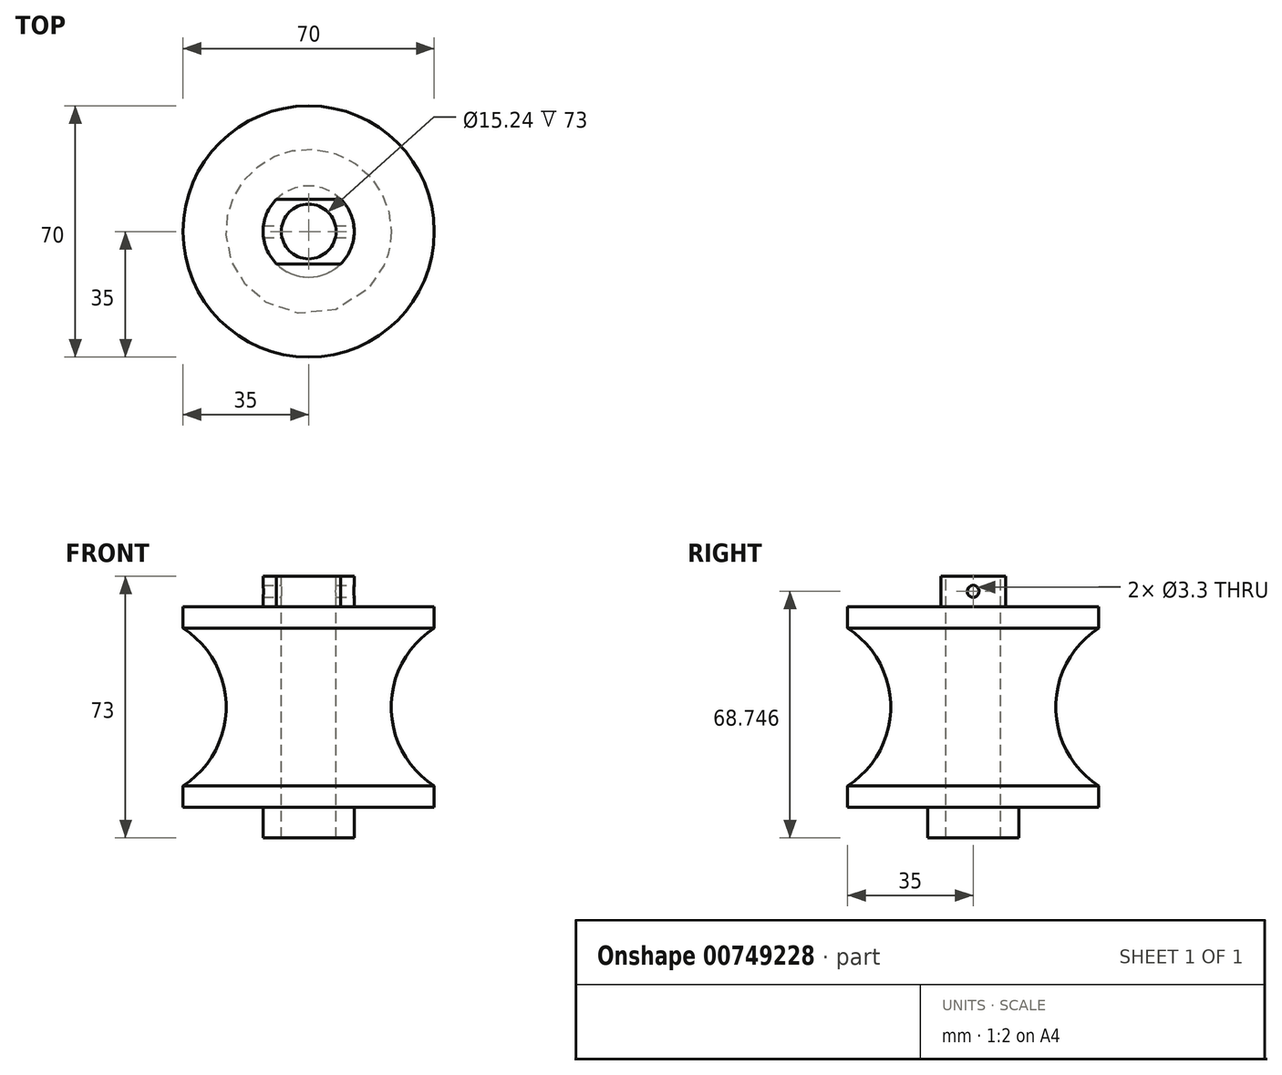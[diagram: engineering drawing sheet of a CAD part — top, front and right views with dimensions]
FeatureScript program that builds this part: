
annotation { "Feature Type Name" : "Feature", "Feature Type Description" : "" }
export const myFeature = defineFeature(function(context is Context, id is Id, definition is map)
    precondition{}
    {
        {
            var Q0;
            Q0=qCreatedBy(makeId("Front.planeOp"),FACE);
            var sketch = newSketch(context, id + "F0", { "sketchPlane" : qUnion([Q0])});
            skLineSegment(sketch, "E0", {"start": v(0, 27.87) * mm, "end": v(0, -28.13) * mm});
            skLineSegment(sketch, "E1", {"start": v(0, 27.87) * mm, "end": v(-35, 27.87) * mm});
            skLineSegment(sketch, "E2", {"start": v(-35, 27.87) * mm, "end": v(-35, 21.87) * mm});
            skLineSegment(sketch, "E3", {"start": v(-35, -22.13) * mm, "end": v(-35, -28.13) * mm});
            skLineSegment(sketch, "E4", {"start": v(-35, -28.13) * mm, "end": v(0, -28.13) * mm});
            skArc(sketch, "E5", {"start": v(-35, -22.13) * mm, "mid": v(-23, -0.13) * mm, "end": v(-35, 21.87) * mm});
            skPoint(sketch, "E6", {"position": v(-23, -0.13) * mm});
            skPoint(sketch, "E7.orphan", {"position": v(0, 36.76) * mm});
            skSolve(sketch);
        }
        {
            var Q0;
            Q0 = qSketchRegion(id + "F0", true);
            var Q1;
            Q1=sQuery(id+"F0.wireOp",EDGE,"E0");
            revolve(context, id + "F1", {"surfaceOperationType" : NewSurfaceOperationType.NEW, "entities" : qUnion([Q0]), "axis" : qUnion([Q1]), "revolveType" : RevolveType.FULL});
        }
        {
            var Q0;
            Q0=makeQuery(id+"F1.opRevolve","SWEPT_FACE",FACE,{"disambiguationData":[OSD([sQuery(id+"F0.wireOp",EDGE,"E1")])]});
            cPlane(context, id + "F2", {"entities" : qUnion([Q0]), "cplaneType" : CPlaneType.OFFSET, "offset" : 8.5 * mm, "width" : 150 * mm, "height" : 150 * mm});
        }
        {
            var Q0;
            Q0=qCreatedBy(id+"F2.planeOp",FACE);
            var sketch = newSketch(context, id + "F3", { "sketchPlane" : qUnion([Q0])});
            skCircle(sketch, "E8", {"center": v(0, 0) * mm, "radius": 12.7 * mm});
            skSolve(sketch);
        }
        {
            var Q0;
            Q0 = qSketchRegion(id + "F3", true);
            extrude(context, id + "F4", {"entities" : qUnion([Q0]), "operationType" : NewBodyOperationType.REMOVE, "endBound" : BoundingType.THROUGH_ALL, "oppositeDirection" : true, "depth" : 25 * mm, "offsetDistance" : 25 * mm});
        }
        {
            var Q0;
            Q0 = qSketchRegion(id + "F3", true);
            extrude(context, id + "F5", {"entities" : qUnion([Q0]), "operationType" : NewBodyOperationType.ADD, "oppositeDirection" : true, "depth" : 73 * mm, "offsetDistance" : 25.4 * mm});
        }
        {
            var Q0;
            Q0=makeQuery(id+"F5.opExtrude","CAP_FACE",FACE,{"disambiguationData":[OSD([sQuery(id+"F3.wireOp",EDGE,"E8")])],"isStart":true});
            var sketch = newSketch(context, id + "F6", { "sketchPlane" : qUnion([Q0])});
            skCircle(sketch, "E9", {"center": v(0, 0) * mm, "radius": 7.62 * mm});
            skSolve(sketch);
        }
        {
            var Q0;
            Q0 = qSketchRegion(id + "F6", true);
            extrude(context, id + "F7", {"entities" : qUnion([Q0]), "operationType" : NewBodyOperationType.REMOVE, "endBound" : BoundingType.THROUGH_ALL, "oppositeDirection" : true, "depth" : 25.4 * mm, "offsetDistance" : 25.4 * mm});
        }
        {
            var Q0;
            Q0=makeQuery(id+"F5.opExtrude","CAP_FACE",FACE,{"disambiguationData":[OSD([sQuery(id+"F3.wireOp",EDGE,"E8")])],"isStart":true});
            var sketch = newSketch(context, id + "F8", { "sketchPlane" : qUnion([Q0])});
            skLineSegment(sketch, "E10.bottom", {"start": v(15, -9) * mm, "end": v(-15, -9) * mm});
            skLineSegment(sketch, "E10.top", {"start": v(15, 9) * mm, "end": v(-15, 9) * mm});
            skPoint(sketch, "E10.middle", {"position": v(0, 0) * mm});
            skLineSegment(sketch, "E11", {"start": v(-15, 9) * mm, "end": v(-15, 16.72) * mm});
            skLineSegment(sketch, "E12", {"start": v(-15, 16.72) * mm, "end": v(15.77, 16.72) * mm});
            skLineSegment(sketch, "E13", {"start": v(15.77, 16.72) * mm, "end": v(15, 9) * mm});
            skLineSegment(sketch, "E14", {"start": v(15, -9) * mm, "end": v(15, -13.4) * mm});
            skLineSegment(sketch, "E15", {"start": v(15, -13.4) * mm, "end": v(-15, -13.4) * mm});
            skLineSegment(sketch, "E16", {"start": v(-15, -13.4) * mm, "end": v(-15, -9) * mm});
            skSolve(sketch);
        }
        {
            var Q0;
            Q0 = qSketchRegion(id + "F8", true);
            extrude(context, id + "F9", {"entities" : qUnion([Q0]), "operationType" : NewBodyOperationType.REMOVE, "oppositeDirection" : true, "depth" : 8.5 * mm, "offsetDistance" : 25 * mm});
        }
        {
            var Q0;
            Q0=qCreatedBy(makeId("Right.planeOp"),FACE);
            cPlane(context, id + "F10", {"entities" : qUnion([Q0]), "cplaneType" : CPlaneType.OFFSET, "offset" : (25.4 / 2) * mm, "width" : 150 * mm, "height" : 150 * mm});
        }
        {
            var Q0;
            Q0=qCreatedBy(id+"F10.planeOp",FACE);
            var sketch = newSketch(context, id + "F11", { "sketchPlane" : qUnion([Q0])});
            skPoint(sketch, "E17", {"position": v(0, 32.12) * mm});
            skSolve(sketch);
        }
        {
            var Q0;
            Q0=sQuery(id+"F11.wireOp",VERTEX,"E17");
            var Q1;
            Q1=makeQuery(id+"F1.opRevolve","SWEPT_BODY",BODY,{"disambiguationData":[OSD([sQuery(id+"F0.wireOp",EDGE,"E0"),sQuery(id+"F0.wireOp",EDGE,"E1"),sQuery(id+"F0.wireOp",EDGE,"E2"),sQuery(id+"F0.wireOp",EDGE,"E3"),sQuery(id+"F0.wireOp",EDGE,"E4"),sQuery(id+"F0.wireOp",EDGE,"E5")])]});
            hole(context, id + "F12", {"style" : HoleStyle.SIMPLE, "endStyle" : HoleEndStyle.BLIND, "standardTappedOrClearance" : lookupTablePath({ "standard" : "ISO", "engagement" : "75%", "pitch" : "0.7 mm", "size" : "M4", "type" : "Tapped" }), "standardBlindInLast" : lookupTablePath({ "standard" : "ISO", "engagement" : "75%", "pitch" : "0.7 mm", "size" : "M4", "type" : "Tapped" }), "holeDiameter" : 3.3 * mm, "majorDiameter" : 4 * mm, "showTappedDepth" : true, "holeDepth" : 30 * mm, "isTappedThrough" : true, "tappedDepth" : 27.9 * mm, "tapClearance" : 3, "startFromSketch" : true, "locations" : qUnion([Q0]), "scope" : qUnion([Q1])});
        }
    });
